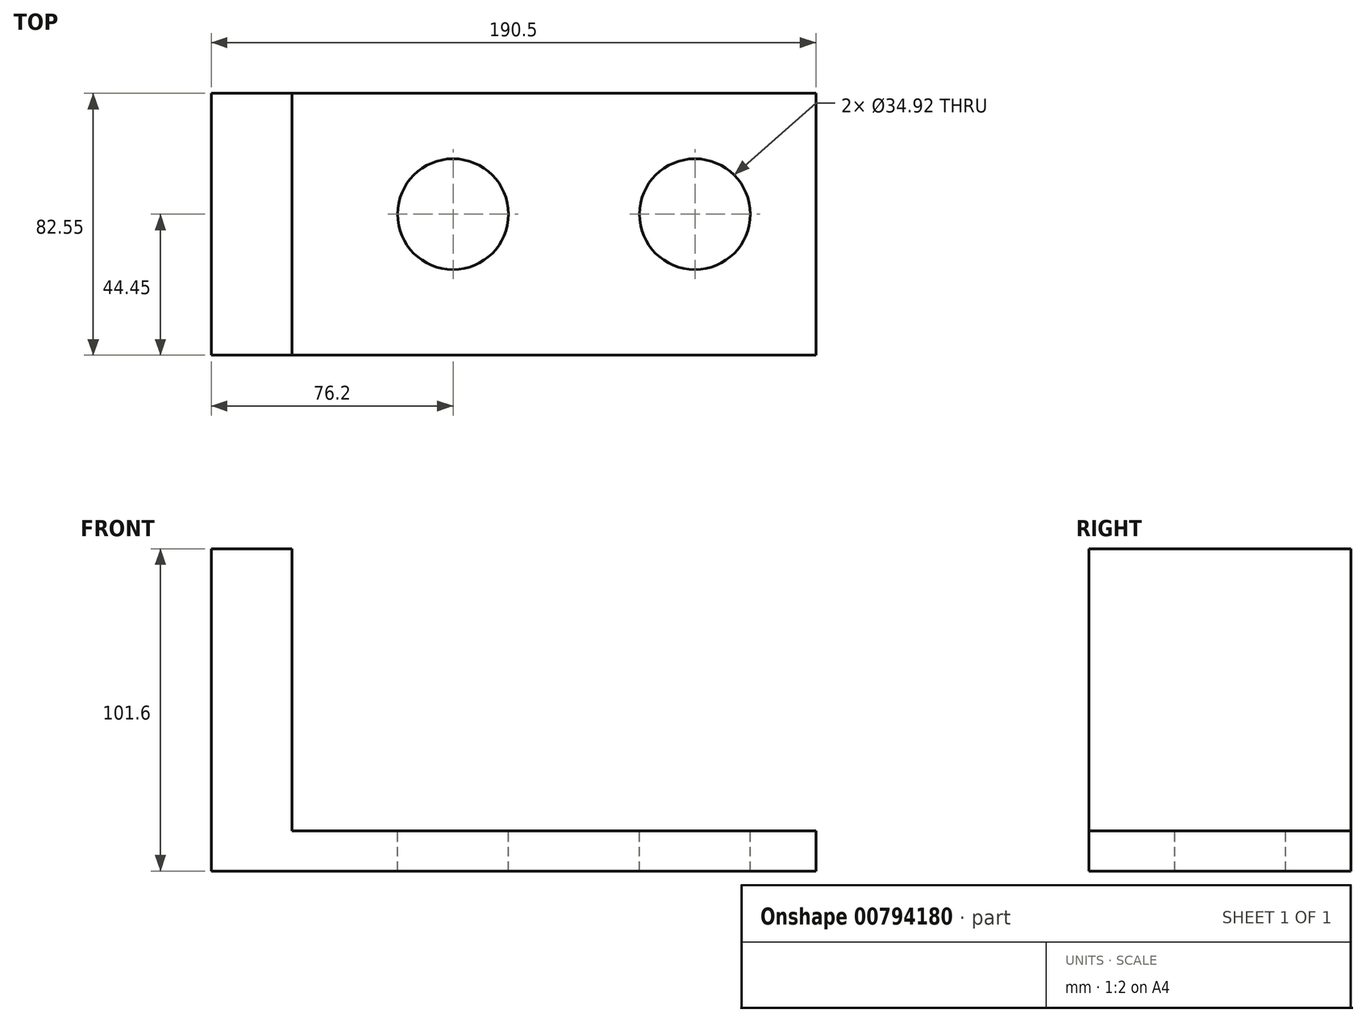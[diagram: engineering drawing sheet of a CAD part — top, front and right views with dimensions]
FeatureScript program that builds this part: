
annotation { "Feature Type Name" : "Feature", "Feature Type Description" : "" }
export const myFeature = defineFeature(function(context is Context, id is Id, definition is map)
    precondition{}
    {
        {
            var Q0;
            Q0=qCreatedBy(makeId("Front.planeOp"),FACE);
            var sketch = newSketch(context, id + "F0", { "sketchPlane" : qUnion([Q0])});
            skLineSegment(sketch, "E0", {"start": v(0, 0) * mm, "end": v(190.5, 0) * mm});
            skLineSegment(sketch, "E1", {"start": v(0, 0) * mm, "end": v(0, 101.6) * mm});
            skLineSegment(sketch, "E2", {"start": v(190.5, 0) * mm, "end": v(190.5, 12.7) * mm});
            skLineSegment(sketch, "E3", {"start": v(190.5, 12.7) * mm, "end": v(25.4, 12.7) * mm});
            skLineSegment(sketch, "E4", {"start": v(25.4, 12.7) * mm, "end": v(25.4, 101.6) * mm});
            skLineSegment(sketch, "E5", {"start": v(25.4, 101.6) * mm, "end": v(0, 101.6) * mm});
            skSolve(sketch);
        }
        {
            var Q0;
            Q0 = qSketchRegion(id + "F0", true);
            extrude(context, id + "F1", {"entities" : qUnion([Q0]), "depth" : 82.55 * mm, "offsetDistance" : 25.4 * mm});
        }
        {
            var Q0;
            Q0=makeQuery(id+"F1.opExtrude","SWEPT_FACE",FACE,{"disambiguationData":[OSD([sQuery(id+"F0.wireOp",EDGE,"E3")])]});
            var sketch = newSketch(context, id + "F2", { "sketchPlane" : qUnion([Q0])});
            skLineSegment(sketch, "E6", {"start": v(190.5, 0) * mm, "end": v(152.4, 0) * mm, "construction": true});
            skLineSegment(sketch, "E7", {"start": v(152.4, 0) * mm, "end": v(76.2, 0) * mm, "construction": true});
            skLineSegment(sketch, "E8", {"start": v(190.5, 0) * mm, "end": v(190.5, -38.1) * mm, "construction": true});
            skLineSegment(sketch, "E9", {"start": v(190.5, -38.1) * mm, "end": v(152.4, -38.1) * mm, "construction": true});
            skLineSegment(sketch, "E10", {"start": v(76.2, 0) * mm, "end": v(76.2, -38.1) * mm, "construction": true});
            skCircle(sketch, "E11", {"center": v(76.2, -38.1) * mm, "radius": 17.46 * mm});
            skCircle(sketch, "E12", {"center": v(152.4, -38.1) * mm, "radius": 17.46 * mm});
            skSolve(sketch);
        }
        {
            var Q0;
            Q0 = qSketchRegion(id + "F2", true);
            extrude(context, id + "F3", {"entities" : qUnion([Q0]), "operationType" : NewBodyOperationType.REMOVE, "oppositeDirection" : true, "depth" : 25.4 * mm, "offsetDistance" : 25.4 * mm});
        }
    });
